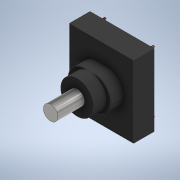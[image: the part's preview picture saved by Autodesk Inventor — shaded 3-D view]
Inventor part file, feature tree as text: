
AUTODESK INVENTOR PART (.ipt)
format: ipt  version: 2020 (Build 240168000, 168)  size: 153,088 bytes
history: native  units: mm
features: extrude x5, sketch x5, fillet x1
ambient origin geometry x8: Origin, YZ Plane, XZ Plane, XY Plane, X Axis, Y Axis, Z Axis, Center Point
bodies: Solid1 (feature_tree)
feature tree (11):
  extrude  "Extrusion1"  Depth=29.7mm
  extrude  "Extrusion2"  Depth=17.6mm
  fillet  "Fillet1"  Radius=13.7mm
  extrude  "Extrusion3"  Depth=6.8mm
  extrude  "Extrusion4"  Depth=5.0mm TaperAngle=0.0deg
  extrude  "Extrusion5"  Depth=11.0mm TaperAngle=0.0deg
  sketch  "Sketch1"  dims[d0=26.5mm d1=29.7mm]
  sketch  "Sketch2"  dims[d2=8.5mm d3=0.0mm d4=17.6mm d5=13.7mm]
  sketch  "Sketch3"  dims[d6=5.0mm d7=0.0mm d8=6.8mm]
  sketch  "Sketch4"  dims[d9=13.65mm d10=5.0mm d11=0.0mm]
  sketch  "Sketch5"  dims[d12=6.0mm d13=11.0mm d14=0.0mm d15=20.0mm d16=25.0mm d18=0.8mm d19=0.8mm d20=0.8mm d21=0.8mm d22=3.0mm d23=0.0mm]
